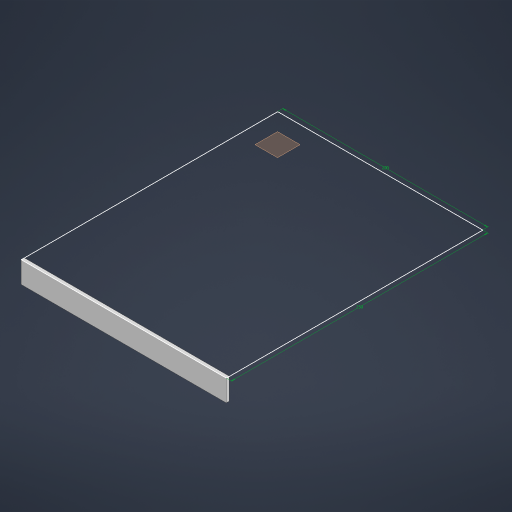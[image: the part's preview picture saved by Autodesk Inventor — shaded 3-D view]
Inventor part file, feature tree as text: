
AUTODESK INVENTOR PART (.ipt)
format: ipt  version: 2023 (Build 270158000, 158)  size: 236,544 bytes
history: native  units: mm
features: extrude x5, sketch x3, other x2, shell x1, plane x1
ambient origin geometry x8: Origin, YZ Plane, XZ Plane, XY Plane, X Axis, Y Axis, Z Axis, Center Point
bodies: Body1 (feature_tree)
feature tree (12):
  other  "block"
  extrude  "ext_block"  Depth=200.0mm
  shell  "Shell2"  Thickness=12.0mm
  extrude  "holes"  Depth=25.0mm
  extrude  "pwr_button_hole"  Depth=3.0mm
  plane  "Work Plane1"
  extrude  "back_cover_cut"  Depth=3.0mm
  extrude  "Extrusion8"  Depth=3.0mm
  other  "lines_base"
  sketch  "Sketch4"  dims[d0=200.0mm d1=250.0mm d2=12.0mm]
  sketch  "Sketch5"  dims[d3=12.0mm d4=25.0mm]
  sketch  "Sketch8"  dims[d5=17.0mm d6=17.0mm d7=25.0mm d8=75.0mm d9=80.0mm d10=65.0mm d11=60.0mm d12=6.0mm d13=84.0mm d14=90.0deg d15=25.0mm d16=125.0mm d17=70.0mm d19=14.0mm d20=10.0mm d22=10.0mm d24=5.0mm d25=10.0mm d26=65.0mm d27=95.0mm d31=200.0mm d32=250.0mm d35=24.0mm d36=0.0mm d37=3.0mm d38=24.0mm d39=0.0mm d40=19.0mm d41=13.0mm d42=4.0mm d43=12.0mm d44=24.0mm d45=0.0mm d49=0.0mm d50=0.0mm d62=0.0mm d63=0.0mm d33=0.5mm d34=0.872665mm d64=0.5mm d65=0.872665mm]
